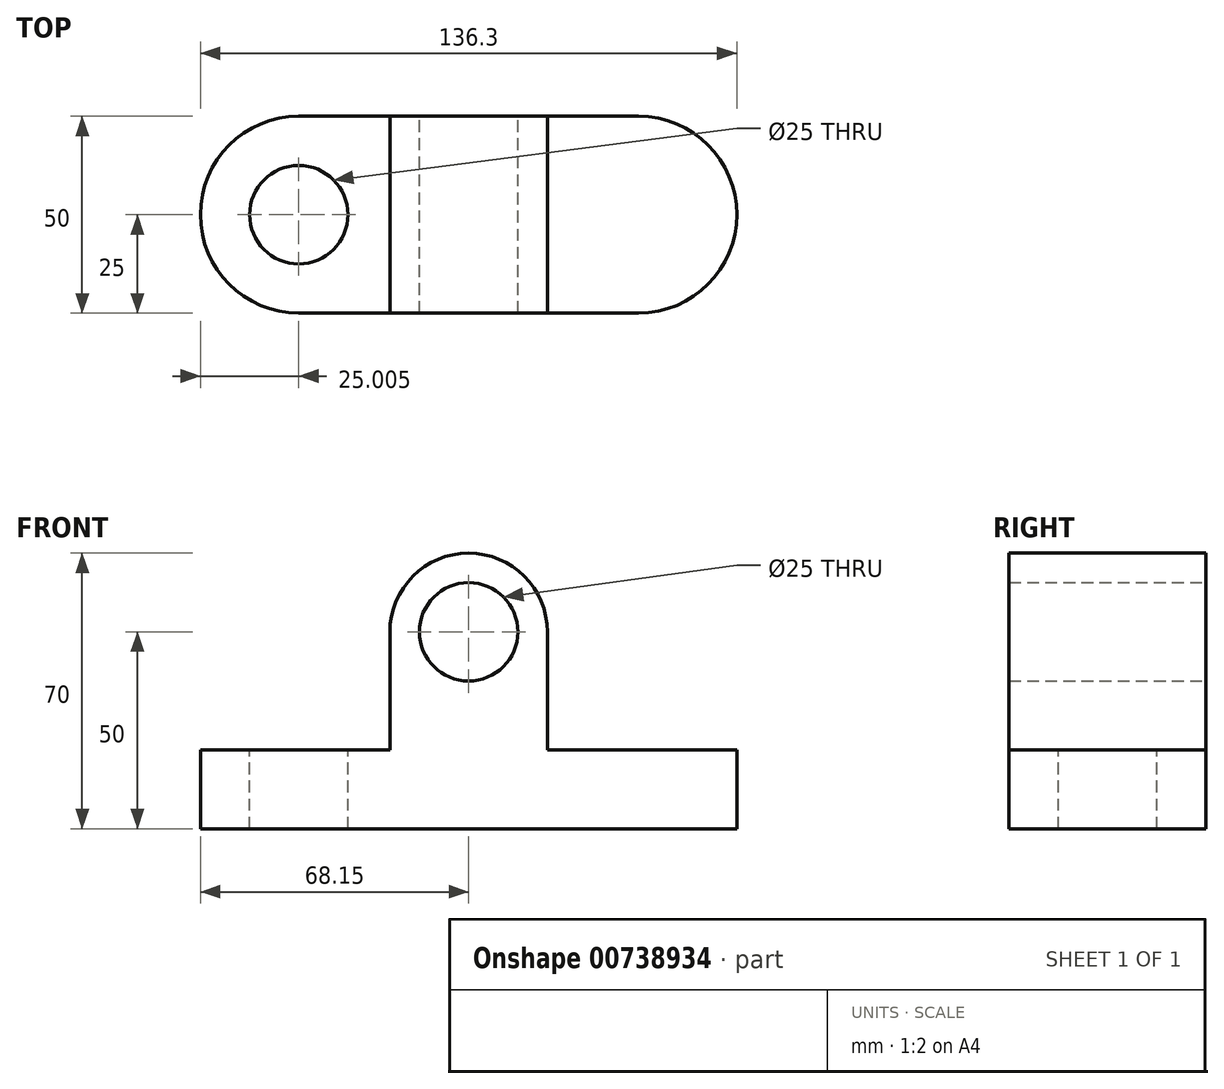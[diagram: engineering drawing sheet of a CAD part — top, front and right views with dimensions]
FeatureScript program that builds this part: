
annotation { "Feature Type Name" : "Feature", "Feature Type Description" : "" }
export const myFeature = defineFeature(function(context is Context, id is Id, definition is map)
    precondition{}
    {
        {
            var Q0;
            Q0=qCreatedBy(makeId("Front.planeOp"),FACE);
            var sketch = newSketch(context, id + "F0", { "sketchPlane" : qUnion([Q0])});
            skLineSegment(sketch, "E0", {"start": v(-20, 0) * mm, "end": v(20, 0) * mm});
            skLineSegment(sketch, "E1", {"start": v(-20, 0) * mm, "end": v(-20, 20) * mm, "construction": true});
            skLineSegment(sketch, "E2", {"start": v(-43.15, 0) * mm, "end": v(43.15, 0) * mm});
            skLineSegment(sketch, "E3", {"start": v(-43.15, 0) * mm, "end": v(-43.15, 20) * mm});
            skLineSegment(sketch, "E4", {"start": v(-43.15, 20) * mm, "end": v(-20, 20) * mm});
            skLineSegment(sketch, "E5.MirrorCS", {"start": v(43.15, 20) * mm, "end": v(20, 20) * mm});
            skLineSegment(sketch, "E6.MirrorCS", {"start": v(43.15, 0) * mm, "end": v(43.15, 20) * mm});
            skLineSegment(sketch, "E7.MirrorCS", {"start": v(20, 0) * mm, "end": v(20, 20) * mm, "construction": true});
            skLineSegment(sketch, "E8", {"start": v(-20, 20) * mm, "end": v(-20, 50) * mm});
            skLineSegment(sketch, "E9", {"start": v(20, 20) * mm, "end": v(20, 50) * mm});
            skLineSegment(sketch, "E10", {"start": v(20, 50) * mm, "end": v(-20, 50) * mm});
            skSolve(sketch);
        }
        {
            var Q0;
            Q0=qCreatedBy(makeId("Top.planeOp"),FACE);
            var sketch = newSketch(context, id + "F1", { "sketchPlane" : qUnion([Q0])});
            skArc(sketch, "E11", {"start": v(-43.15, 25) * mm, "mid": v(-68.15, 0) * mm, "end": v(-43.15, -25) * mm});
            skLineSegment(sketch, "E12", {"start": v(-43.15, 35.74) * mm, "end": v(-43.15, -47.5) * mm, "construction": true});
            skLineSegment(sketch, "E13", {"start": v(-43.15, 25) * mm, "end": v(-43.15, -25) * mm});
            skSolve(sketch);
        }
        {
            var Q0;
            {var subQ0=sQuery(id+"F0.wireOp",EDGE,"E3");Q0=makeQuery(id+"F0.imprint","IMPRINT",FACE,{"disambiguationData":[TD([[makeQuery(id+"F0.imprint","IMPRINT",EDGE,{"derivedFrom":subQ0}),-1.0]])]});}
            extrude(context, id + "F2", {"entities" : qUnion([Q0]), "endBound" : BoundingType.SYMMETRIC, "depth" : 50 * mm, "offsetDistance" : 25 * mm});
        }
        {
            var Q0;
            Q0=makeQuery(id+"F1.imprint","IMPRINT",FACE,{"disambiguationData":[TD([[makeQuery(id+"F1.imprint","IMPRINT",EDGE,{"derivedFrom":sQuery(id+"F1.wireOp",EDGE,"E11")}),1.0]])]});
            extrude(context, id + "F3", {"entities" : qUnion([Q0]), "operationType" : NewBodyOperationType.ADD, "depth" : 20 * mm, "offsetDistance" : 25 * mm});
        }
        {
            var Q0;
            Q0=makeQuery(id+"F2.opExtrude","SWEPT_BODY",BODY,{"disambiguationData":[OSD([sQuery(id+"F0.wireOp",EDGE,"E2"),sQuery(id+"F0.wireOp",EDGE,"E3"),sQuery(id+"F0.wireOp",EDGE,"E4"),sQuery(id+"F0.wireOp",EDGE,"E5.MirrorCS"),sQuery(id+"F0.wireOp",EDGE,"E6.MirrorCS"),sQuery(id+"F0.wireOp",EDGE,"E8"),sQuery(id+"F0.wireOp",EDGE,"E9"),sQuery(id+"F0.wireOp",EDGE,"E10")])]});
            var Q1;
            Q1=qCreatedBy(makeId("Right.planeOp"),FACE);
            mirror(context, id + "F4", {"operationType" : NewBodyOperationType.ADD, "entities" : qUnion([Q0]), "mirrorPlane" : qUnion([Q1])});
        }
        {
            var Q0;
            Q0=makeQuery(id+"F2.opExtrude","CAP_FACE",FACE,{"disambiguationData":[OSD([sQuery(id+"F0.wireOp",EDGE,"E2"),sQuery(id+"F0.wireOp",EDGE,"E3"),sQuery(id+"F0.wireOp",EDGE,"E4"),sQuery(id+"F0.wireOp",EDGE,"E5.MirrorCS"),sQuery(id+"F0.wireOp",EDGE,"E6.MirrorCS"),sQuery(id+"F0.wireOp",EDGE,"E8"),sQuery(id+"F0.wireOp",EDGE,"E9"),sQuery(id+"F0.wireOp",EDGE,"E10")])],"isStart":false});
            var sketch = newSketch(context, id + "F5", { "sketchPlane" : qUnion([Q0])});
            skArc(sketch, "E14", {"start": v(20, 50) * mm, "mid": v(0, 70) * mm, "end": v(-20, 50) * mm});
            skSolve(sketch);
        }
        {
            var Q0;
            Q0=makeQuery(id+"F5.imprint","IMPRINT",FACE,{"disambiguationData":[TD([[makeQuery(id+"F5.imprint","IMPRINT",EDGE,{"derivedFrom":sQuery(id+"F5.wireOp",EDGE,"E14")}),1.0]])]});
            extrude(context, id + "F6", {"entities" : qUnion([Q0]), "operationType" : NewBodyOperationType.ADD, "oppositeDirection" : true, "depth" : 50 * mm, "offsetDistance" : 25 * mm});
        }
        {
            var Q0;
            Q0=makeQuery(id+"F3.boolean.opBoolean","MERGE",FACE,{"derivedFrom":[makeQuery(id+"F2.opExtrude","SWEPT_FACE",FACE,{"disambiguationData":[OSD([sQuery(id+"F0.wireOp",EDGE,"E4")])]}),makeQuery(id+"F3.opExtrude","CAP_FACE",FACE,{"disambiguationData":[OSD([sQuery(id+"F1.wireOp",EDGE,"E11"),sQuery(id+"F1.wireOp",EDGE,"E13")])],"isStart":false})]});
            var sketch = newSketch(context, id + "F7", { "sketchPlane" : qUnion([Q0])});
            skCircle(sketch, "E15", {"center": v(-43.15, 0) * mm, "radius": 12.5 * mm});
            skCircle(sketch, "E16.MirrorC", {"center": v(43.15, 0) * mm, "radius": 12.5 * mm});
            skSolve(sketch);
        }
        {
            var Q0;
            {var subQ0=sQuery(id+"F0.wireOp",EDGE,"E10");Q0=makeQuery(id+"F6.boolean.opBoolean","MERGE",FACE,{"derivedFrom":[makeQuery(id+"F2.opExtrude","CAP_FACE",FACE,{"disambiguationData":[OSD([sQuery(id+"F0.wireOp",EDGE,"E2"),sQuery(id+"F0.wireOp",EDGE,"E3"),sQuery(id+"F0.wireOp",EDGE,"E4"),sQuery(id+"F0.wireOp",EDGE,"E5.MirrorCS"),sQuery(id+"F0.wireOp",EDGE,"E6.MirrorCS"),sQuery(id+"F0.wireOp",EDGE,"E8"),sQuery(id+"F0.wireOp",EDGE,"E9"),subQ0])],"isStart":true}),makeQuery(id+"F6.opExtrude","CAP_FACE",FACE,{"disambiguationData":[OSD([subQ0,sQuery(id+"F5.wireOp",EDGE,"E14")])],"isStart":false})]});}
            var sketch = newSketch(context, id + "F8", { "sketchPlane" : qUnion([Q0])});
            skCircle(sketch, "E17", {"center": v(0, 50) * mm, "radius": 12.5 * mm});
            skSolve(sketch);
        }
        {
            var Q0;
            Q0=makeQuery(id+"F8.imprint","IMPRINT",FACE,{"disambiguationData":[TD([[makeQuery(id+"F8.imprint","IMPRINT",EDGE,{"derivedFrom":sQuery(id+"F8.wireOp",EDGE,"E17")}),1.0]])]});
            extrude(context, id + "F9", {"entities" : qUnion([Q0]), "operationType" : NewBodyOperationType.REMOVE, "endBound" : BoundingType.SYMMETRIC, "oppositeDirection" : true, "depth" : 108.8 * mm, "offsetDistance" : 25 * mm});
        }
        {
            var Q0;
            Q0=makeQuery(id+"F7.imprint","IMPRINT",FACE,{"disambiguationData":[TD([[makeQuery(id+"F7.imprint","IMPRINT",EDGE,{"derivedFrom":sQuery(id+"F7.wireOp",EDGE,"E16.MirrorC")}),-1.0]])]});
            var Q1;
            Q1=makeQuery(id+"F7.imprint","IMPRINT",FACE,{"disambiguationData":[TD([[makeQuery(id+"F7.imprint","IMPRINT",EDGE,{"derivedFrom":sQuery(id+"F7.wireOp",EDGE,"E15")}),1.0]])]});
            extrude(context, id + "F10", {"entities" : qUnion([Q0, Q1]), "operationType" : NewBodyOperationType.REMOVE, "oppositeDirection" : true, "depth" : 25 * mm, "offsetDistance" : 25 * mm});
        }
    });
